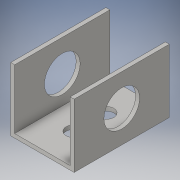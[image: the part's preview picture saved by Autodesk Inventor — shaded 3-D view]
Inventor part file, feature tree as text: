
AUTODESK INVENTOR PART (.ipt)
format: ipt  version: 2016 (Build 200138000, 138)  size: 128,512 bytes
history: native  units: in
note: dims shown in document units (in); Inventor stores cm internally (conversion verified against a paired STEP export)
features: sketch x3, extrude x3
ambient origin geometry x8: Origin, YZ Plane, XZ Plane, XY Plane, X Axis, Y Axis, Z Axis, Center Point
bodies: Body1 (feature_tree)
feature tree (6):
  sketch  "Sketch1"  dims[d0=2.0in d1=3.0in]
  extrude  "Extrusion3"  Depth=3.0in
  extrude  "Extrusion4"  Depth=1.0in
  extrude  "Extrusion6"  Depth=2.0in
  sketch  "Sketch5"  dims[d13=1.0in d14=1.0in]
  sketch  "Sketch6"  dims[d15=1.0in d16=1.0in d17=0.5in d18=0.5in d19=0.125in d20=0.0in d21=0.125in d22=0.125in d23=3.0in d24=3.0in d25=1.875in d26=0.0in d27=1.124in d28=1.5in d29=1.0in d32=2.0in d33=0.0in]
